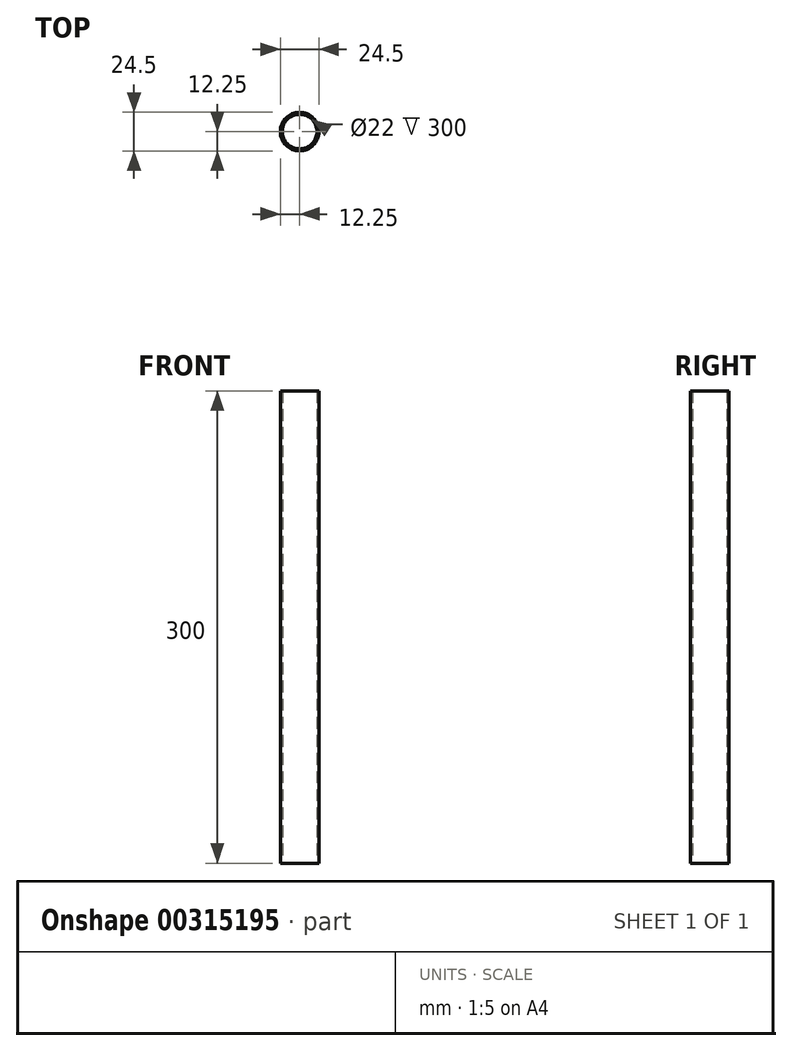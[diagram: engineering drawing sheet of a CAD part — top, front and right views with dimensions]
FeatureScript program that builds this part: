
annotation { "Feature Type Name" : "Feature", "Feature Type Description" : "" }
export const myFeature = defineFeature(function(context is Context, id is Id, definition is map)
    precondition{}
    {
        {
            var Q0;
            Q0=qCreatedBy(makeId("Top.planeOp"),FACE);
            var sketch = newSketch(context, id + "F0", { "sketchPlane" : qUnion([Q0])});
            skCircle(sketch, "E0", {"center": v(0, 0) * mm, "radius": 12.25 * mm});
            skCircle(sketch, "E1", {"center": v(0, 0) * mm, "radius": 11 * mm});
            skSolve(sketch);
        }
        {
            var Q0;
            Q0=qSketchRegion(id+"F0",true);
            extrude(context, id + "F1", {"entities" : qUnion([Q0]), "depth" : 300 * mm});
        }
    });
